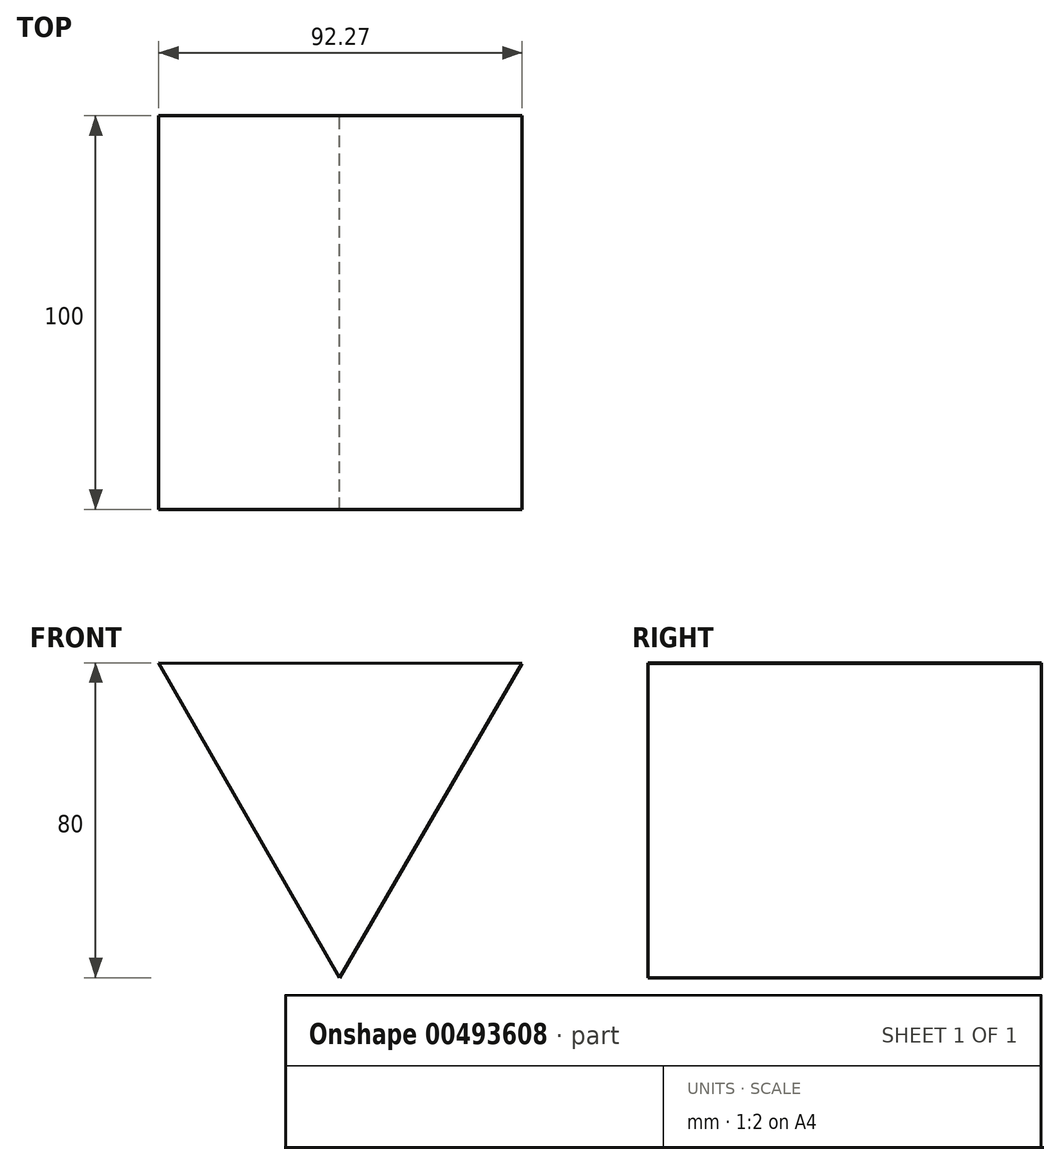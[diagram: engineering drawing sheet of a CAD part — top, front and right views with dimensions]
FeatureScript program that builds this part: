
annotation { "Feature Type Name" : "Feature", "Feature Type Description" : "" }
export const myFeature = defineFeature(function(context is Context, id is Id, definition is map)
    precondition{}
    {
        {
            var Q0;
            Q0=qCreatedBy(makeId("Front.planeOp"),FACE);
            var sketch = newSketch(context, id + "F0", { "sketchPlane" : qUnion([Q0])});
            skCircle(sketch, "E0.cCircle", {"center": v(0, 0) * mm, "radius": 53.27 * mm, "construction": true});
            skLineSegment(sketch, "E0.0", {"start": v(46.19, 26.54) * mm, "end": v(-0.11, -53.27) * mm});
            skLineSegment(sketch, "E0.1", {"start": v(-0.11, -53.27) * mm, "end": v(-46.08, 26.73) * mm});
            skLineSegment(sketch, "E0.2", {"start": v(-46.08, 26.73) * mm, "end": v(46.19, 26.54) * mm});
            skSolve(sketch);
        }
        {
            var Q0;
            Q0=makeQuery(id+"F0.imprint","IMPRINT",FACE,{"disambiguationData":[TD([[makeQuery(id+"F0.imprint","IMPRINT",EDGE,{"derivedFrom":sQuery(id+"F0.wireOp",EDGE,"E0.0")}),-1.0]])]});
            extrude(context, id + "F1", {"entities" : qUnion([Q0]), "endBound" : BoundingType.SYMMETRIC, "depth" : 100 * mm});
        }
    });
